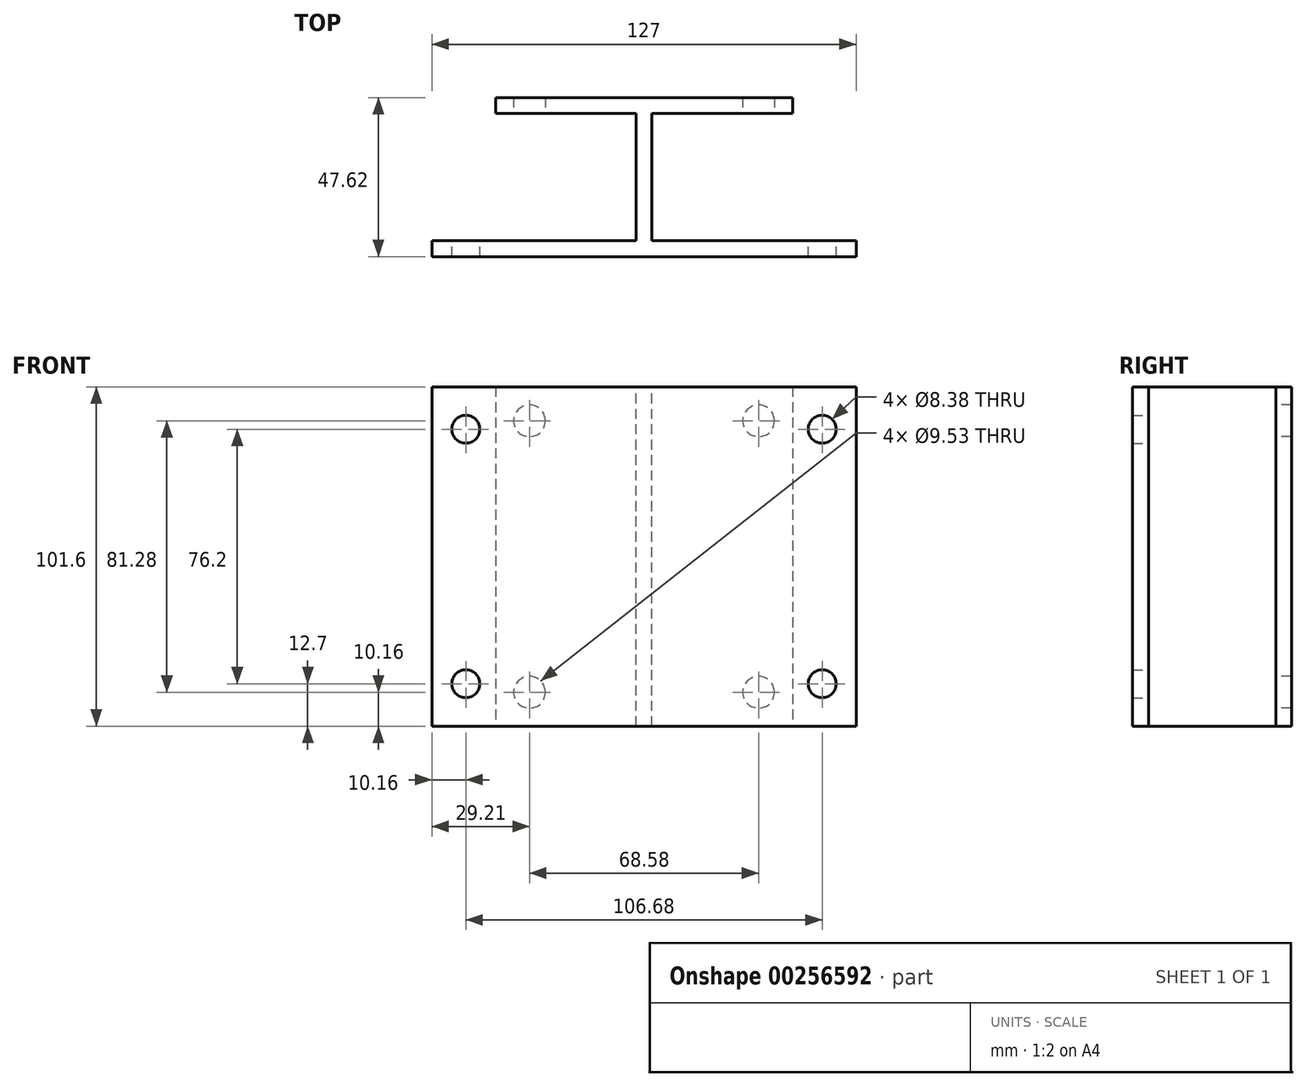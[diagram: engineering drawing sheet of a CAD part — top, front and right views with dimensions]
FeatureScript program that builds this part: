
annotation { "Feature Type Name" : "Feature", "Feature Type Description" : "" }
export const myFeature = defineFeature(function(context is Context, id is Id, definition is map)
    precondition{}
    {
        {
            var Q0;
            Q0=qCreatedBy(makeId("Front.planeOp"),FACE);
            var sketch = newSketch(context, id + "F0", { "sketchPlane" : qUnion([Q0])});
            skLineSegment(sketch, "E0.bottom", {"start": v(63.5, -50.8) * mm, "end": v(-63.5, -50.8) * mm});
            skLineSegment(sketch, "E0.top", {"start": v(63.5, 50.8) * mm, "end": v(-63.5, 50.8) * mm});
            skLineSegment(sketch, "E0.left", {"start": v(63.5, -50.8) * mm, "end": v(63.5, 50.8) * mm});
            skLineSegment(sketch, "E0.right", {"start": v(-63.5, -50.8) * mm, "end": v(-63.5, 50.8) * mm});
            skPoint(sketch, "E0.middle", {"position": v(0, 0) * mm});
            skCircle(sketch, "E1", {"center": v(-53.34, 38.1) * mm, "radius": 4.2 * mm});
            skCircle(sketch, "E2.MirrorC", {"center": v(53.34, 38.1) * mm, "radius": 4.2 * mm});
            skCircle(sketch, "E3.MirrorC", {"center": v(53.34, -38.1) * mm, "radius": 4.2 * mm});
            skCircle(sketch, "E4.MirrorC", {"center": v(-53.34, -38.1) * mm, "radius": 4.2 * mm});
            skSolve(sketch);
        }
        {
            var Q0;
            Q0=makeQuery(id+"F0.imprint","IMPRINT",FACE,{"disambiguationData":[TD([[makeQuery(id+"F0.imprint","IMPRINT",EDGE,{"derivedFrom":sQuery(id+"F0.wireOp",EDGE,"E0.bottom")}),-1.0]])]});
            extrude(context, id + "F1", {"entities" : qUnion([Q0]), "depth" : 4.76 * mm});
        }
        {
            var Q0;
            Q0=makeQuery(id+"F1.opExtrude","CAP_FACE",FACE,{"disambiguationData":[OSD([sQuery(id+"F0.wireOp",EDGE,"E0.bottom"),sQuery(id+"F0.wireOp",EDGE,"E0.top"),sQuery(id+"F0.wireOp",EDGE,"E0.left"),sQuery(id+"F0.wireOp",EDGE,"E0.right"),sQuery(id+"F0.wireOp",EDGE,"E1"),sQuery(id+"F0.wireOp",EDGE,"E2.MirrorC"),sQuery(id+"F0.wireOp",EDGE,"E3.MirrorC"),sQuery(id+"F0.wireOp",EDGE,"E4.MirrorC")])],"isStart":true});
            var sketch = newSketch(context, id + "F2", { "sketchPlane" : qUnion([Q0])});
            skLineSegment(sketch, "E5.bottom", {"start": v(-2.38, -50.8) * mm, "end": v(2.38, -50.8) * mm});
            skLineSegment(sketch, "E5.top", {"start": v(-2.38, 50.8) * mm, "end": v(2.38, 50.8) * mm});
            skLineSegment(sketch, "E5.left", {"start": v(-2.38, -50.8) * mm, "end": v(-2.38, 50.8) * mm});
            skLineSegment(sketch, "E5.right", {"start": v(2.38, -50.8) * mm, "end": v(2.38, 50.8) * mm});
            skPoint(sketch, "E5.middle", {"position": v(0, 0) * mm});
            skSolve(sketch);
        }
        {
            var Q0;
            Q0 = qSketchRegion(id + "F2", true);
            extrude(context, id + "F3", {"entities" : qUnion([Q0]), "operationType" : NewBodyOperationType.ADD, "depth" : 38.1 * mm});
        }
        {
            var Q0;
            Q0=makeQuery(id+"F3.opExtrude","CAP_FACE",FACE,{"disambiguationData":[OSD([sQuery(id+"F2.wireOp",EDGE,"E5.bottom"),sQuery(id+"F2.wireOp",EDGE,"E5.top"),sQuery(id+"F2.wireOp",EDGE,"E5.left"),sQuery(id+"F2.wireOp",EDGE,"E5.right")])],"isStart":false});
            var sketch = newSketch(context, id + "F4", { "sketchPlane" : qUnion([Q0])});
            skLineSegment(sketch, "E6.bottom", {"start": v(44.45, 50.8) * mm, "end": v(-44.45, 50.8) * mm});
            skLineSegment(sketch, "E6.top", {"start": v(44.45, -50.8) * mm, "end": v(-44.45, -50.8) * mm});
            skLineSegment(sketch, "E6.left", {"start": v(44.45, 50.8) * mm, "end": v(44.45, -50.8) * mm});
            skLineSegment(sketch, "E6.right", {"start": v(-44.45, 50.8) * mm, "end": v(-44.45, -50.8) * mm});
            skPoint(sketch, "E6.middle", {"position": v(0, 0) * mm});
            skCircle(sketch, "E7", {"center": v(-34.3, 40.64) * mm, "radius": 4.76 * mm});
            skCircle(sketch, "E8.MirrorC", {"center": v(34.3, 40.64) * mm, "radius": 4.76 * mm});
            skCircle(sketch, "E9.MirrorC", {"center": v(34.3, -40.64) * mm, "radius": 4.76 * mm});
            skCircle(sketch, "E10.MirrorC", {"center": v(-34.3, -40.64) * mm, "radius": 4.76 * mm});
            skSolve(sketch);
        }
        {
            var Q0;
            Q0 = qSketchRegion(id + "F4", true);
            extrude(context, id + "F5", {"entities" : qUnion([Q0]), "operationType" : NewBodyOperationType.ADD, "depth" : 4.76 * mm});
        }
    });
